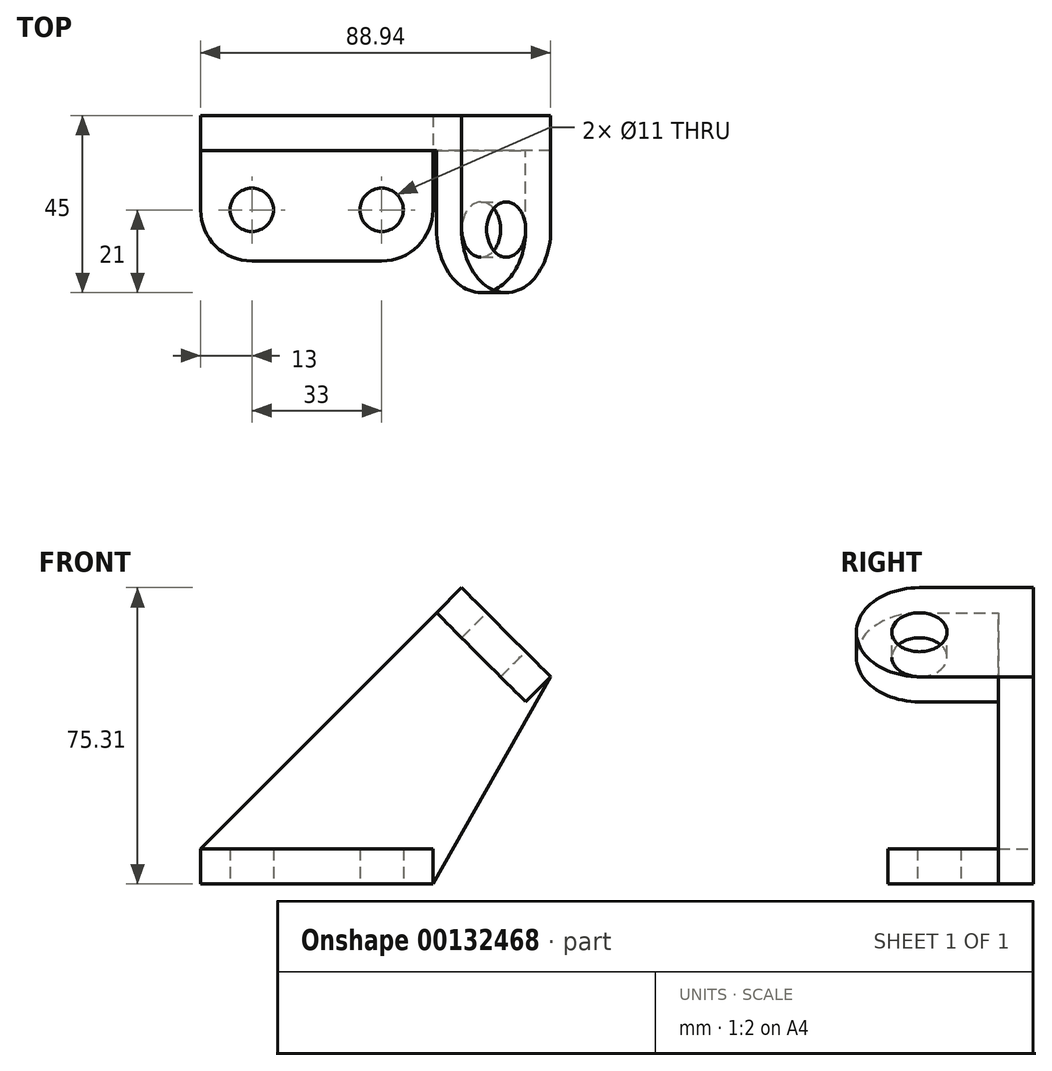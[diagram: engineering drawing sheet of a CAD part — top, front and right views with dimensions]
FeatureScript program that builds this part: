
annotation { "Feature Type Name" : "Feature", "Feature Type Description" : "" }
export const myFeature = defineFeature(function(context is Context, id is Id, definition is map)
    precondition{}
    {
        {
            var Q0;
            Q0=qCreatedBy(makeId("Top.planeOp"),FACE);
            var sketch = newSketch(context, id + "F0", { "sketchPlane" : qUnion([Q0])});
            skLineSegment(sketch, "E0", {"start": v(-29.5, 0) * mm, "end": v(-29.5, 24) * mm});
            skLineSegment(sketch, "E1", {"start": v(-29.5, 24) * mm, "end": v(0, 24) * mm});
            skLineSegment(sketch, "E2", {"start": v(0, 24) * mm, "end": v(29.5, 24) * mm});
            skLineSegment(sketch, "E3", {"start": v(29.5, 24) * mm, "end": v(29.5, 0) * mm});
            skArc(sketch, "E4", {"start": v(-29.5, 0) * mm, "mid": v(-25.7, -9.2) * mm, "end": v(-16.5, -13) * mm});
            skArc(sketch, "E5", {"start": v(16.5, -13) * mm, "mid": v(25.7, -9.2) * mm, "end": v(29.5, 0) * mm});
            skLineSegment(sketch, "E6", {"start": v(-16.5, -13) * mm, "end": v(16.5, -13) * mm});
            skCircle(sketch, "E7", {"center": v(-16.5, 0) * mm, "radius": 5.5 * mm});
            skCircle(sketch, "E8", {"center": v(16.5, 0) * mm, "radius": 5.5 * mm});
            skSolve(sketch);
        }
        {
            var Q0;
            Q0 = qSketchRegion(id + "F0", true);
            extrude(context, id + "F1", {"entities" : qUnion([Q0]), "depth" : 9 * mm});
        }
        {
            var Q0;
            Q0=makeQuery(id+"F1.opExtrude","SWEPT_FACE",FACE,{"disambiguationData":[OSD([sQuery(id+"F0.wireOp",EDGE,"E1"),sQuery(id+"F0.wireOp",EDGE,"E2")])]});
            var sketch = newSketch(context, id + "F2", { "sketchPlane" : qUnion([Q0])});
            skLineSegment(sketch, "E9", {"start": v(29.5, 0) * mm, "end": v(-29.5, 0) * mm});
            skLineSegment(sketch, "E10", {"start": v(29.5, 0) * mm, "end": v(29.5, 9) * mm});
            skLineSegment(sketch, "E11", {"start": v(29.5, 9) * mm, "end": v(-36.81, 75.31) * mm});
            skLineSegment(sketch, "E12", {"start": v(-36.81, 75.31) * mm, "end": v(-48.13, 64) * mm});
            skLineSegment(sketch, "E13", {"start": v(-48.13, 64) * mm, "end": v(-59.44, 52.69) * mm});
            skLineSegment(sketch, "E14", {"start": v(-48.13, 64) * mm, "end": v(-84.25, 64) * mm, "construction": true});
            skLineSegment(sketch, "E15", {"start": v(-59.44, 52.69) * mm, "end": v(-29.5, 0) * mm});
            skSolve(sketch);
        }
        {
            var Q0;
            Q0 = qSketchRegion(id + "F2", true);
            extrude(context, id + "F3", {"entities" : qUnion([Q0]), "operationType" : NewBodyOperationType.ADD, "oppositeDirection" : true, "depth" : 9 * mm});
        }
        {
            var Q0;
            Q0=makeQuery(id+"F3.opExtrude","SWEPT_FACE",FACE,{"disambiguationData":[OSD([sQuery(id+"F2.wireOp",EDGE,"E12"),sQuery(id+"F2.wireOp",EDGE,"E13")])]});
            var sketch = newSketch(context, id + "F4", { "sketchPlane" : qUnion([Q0])});
            skLineSegment(sketch, "E16", {"start": v(24, 27.22) * mm, "end": v(-5, 27.22) * mm});
            skLineSegment(sketch, "E17", {"start": v(-5, 27.22) * mm, "end": v(-5, -4.78) * mm, "construction": true});
            skLineSegment(sketch, "E18", {"start": v(-5, -4.78) * mm, "end": v(24, -4.78) * mm});
            skLineSegment(sketch, "E19", {"start": v(24, -4.78) * mm, "end": v(24, 27.22) * mm});
            skCircle(sketch, "E20", {"center": v(-5, 11.22) * mm, "radius": 7 * mm});
            skArc(sketch, "E21", {"start": v(-5, 27.22) * mm, "mid": v(-21, 11.22) * mm, "end": v(-5, -4.78) * mm});
            skSolve(sketch);
        }
        {
            var Q0;
            Q0 = qSketchRegion(id + "F4", true);
            extrude(context, id + "F5", {"entities" : qUnion([Q0]), "operationType" : NewBodyOperationType.ADD, "oppositeDirection" : true, "depth" : 9 * mm});
        }
    });
